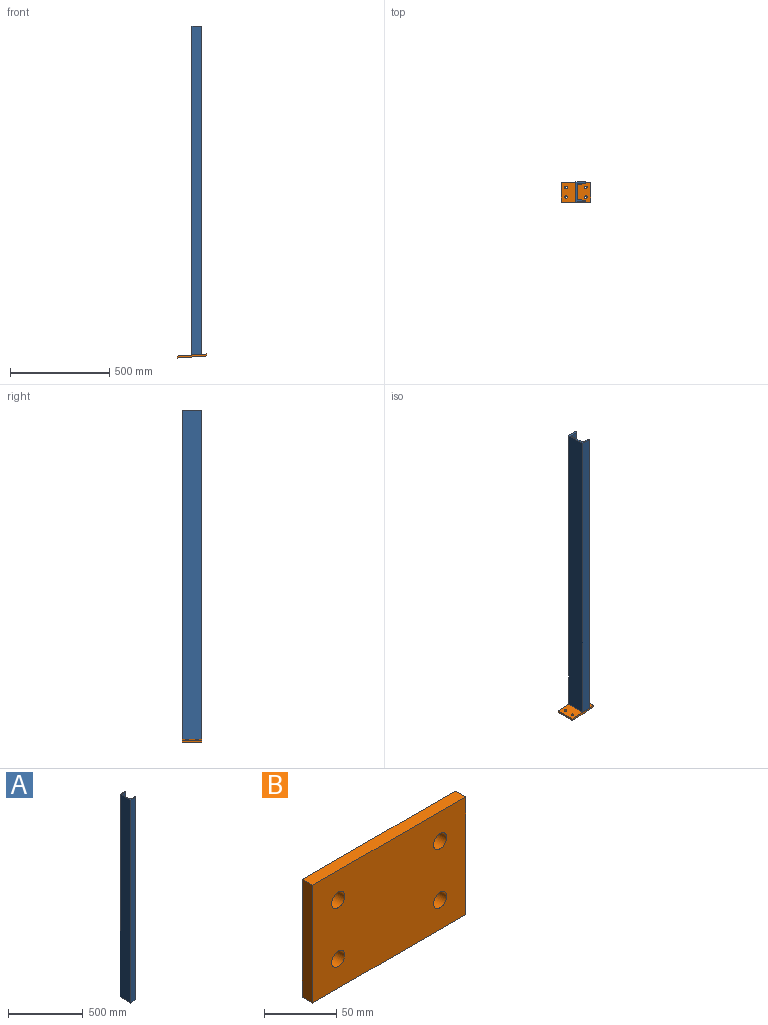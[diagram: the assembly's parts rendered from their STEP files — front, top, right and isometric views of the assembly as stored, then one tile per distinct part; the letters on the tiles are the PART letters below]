
ASSEMBLY  parts=2 mates=1
PART A: 14 faces, bbox 50x100x1658.5 mm
  f0: plane 1658.54x50mm, normal (0,-1,0), area 82841.1mm2, adj f2,f3,f12,f13
  f1: plane 1655.11x3mm, normal (1,0,0), area 4965.3mm2, adj f4,f5,f12,f13
  f2: plane 1655.11x3mm, normal (1,0,0), area 4965.3mm2, adj f0,f11,f12,f13
  f3: plane 1658.54x100mm, normal (-1,0,0), area 165853.9mm2, adj f0,f4,f12,f13
  f4: plane 1658.54x50mm, normal (0,1,0), area 82841.1mm2, adj f1,f3,f12,f13
  f5: cylinder r=4.5mm len=1655.42mm, axis (0,0,1), area 11700.1mm2, adj f1,f6,f12,f13
  f6: plane 1657.54x31mm, normal (0.06,-1,0), area 51457.6mm2, adj f5,f7,f12,f13
  f7: cylinder r=8.5mm len=1658.13mm, axis (0,0,1), area 22136.1mm2, adj f6,f8,f12,f13
  f8: plane 1658.13x64mm, normal (1,0,0), area 106120.1mm2, adj f7,f9,f12,f13
  f9: cylinder r=8.5mm len=1658.13mm, axis (0,0,1), area 22136.1mm2, adj f8,f10,f12,f13
  f10: plane 1657.54x31mm, normal (0.06,1,0), area 51457.6mm2, adj f9,f11,f12,f13
  f11: cylinder r=4.5mm len=1655.42mm, axis (0,0,1), area 11700.1mm2, adj f2,f10,f12,f13
  f12: plane 100x50mm, normal (0,0,1), area 1378.3mm2, adj f0,f1,f2,f3,f4,f5,f6,f7
  f13: plane 100x50mm, normal (0.07,0,-1), area 1381.6mm2, adj f0,f1,f2,f3,f4,f5,f6,f7
PART B: 10 faces, bbox 150x10x100 mm
  f0: plane 150x10mm, normal (0,0,-1), area 1500mm2, adj f1,f7,f8,f9
  f1: plane 100x10mm, normal (1,0,0), area 1000mm2, adj f0,f2,f8,f9
  f2: plane 150x10mm, normal (0,0,1), area 1500mm2, adj f1,f7,f8,f9
  f3: cylinder r=6.5mm len=13mm, axis (0,1,0), area 408.4mm2, adj f8,f9
  f4: cylinder r=6.5mm len=13mm, axis (0,1,0), area 408.4mm2, adj f8,f9
  f5: cylinder r=6.5mm len=13mm, axis (0,1,0), area 408.4mm2, adj f8,f9
  f6: cylinder r=6.5mm len=13mm, axis (0,1,0), area 408.4mm2, adj f8,f9
  f7: plane 100x10mm, normal (-1,0,0), area 1000mm2, adj f0,f2,f8,f9
  f8: plane 150x100mm, normal (0,-1,0), area 14469.1mm2, adj f0,f1,f2,f3,f4,f5,f6,f7
  f9: plane 150x100mm, normal (0,1,0), area 14469.1mm2, adj f0,f1,f2,f3,f4,f5,f6,f7
PLACE A rot(axis=(0,1,0),0deg) t=(490.38,-15.04,-1194.15)mm
PLACE B rot(axis=(-1,-0.03,-0.03),90.1deg) t=(490.74,35.04,-1199.14)mm
MATE fastened A.f13 <-> B.f8  axis (0.07,0,-1) through (490.4,35.04,-1194.15)mm
